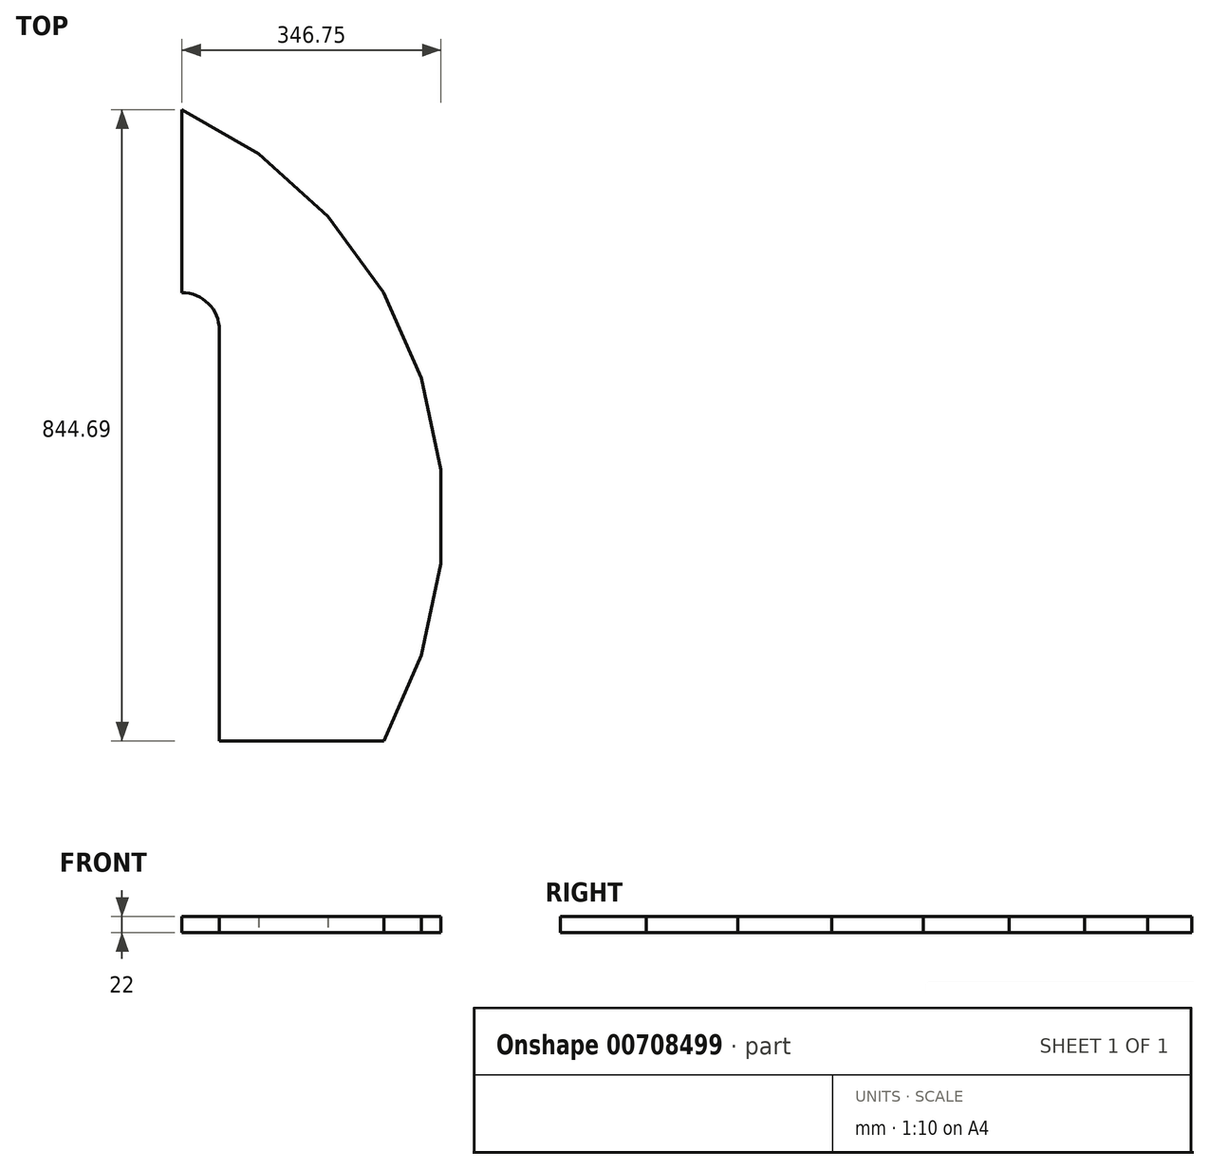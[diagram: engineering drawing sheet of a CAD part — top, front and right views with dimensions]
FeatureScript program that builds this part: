
annotation { "Feature Type Name" : "Feature", "Feature Type Description" : "" }
export const myFeature = defineFeature(function(context is Context, id is Id, definition is map)
    precondition{}
    {
        {
            var Q0;
            Q0=qCreatedBy(makeId("Top.planeOp"),FACE);
            var sketch = newSketch(context, id + "F0", { "sketchPlane" : qUnion([Q0])});
            skLineSegment(sketch, "E0.right", {"start": v(300, -300) * mm, "end": v(300, 250) * mm});
            skPoint(sketch, "E0.middle", {"position": v(0, 0) * mm});
            skPoint(sketch, "E1.end.orphan", {"position": v(-300, -300) * mm});
            skLineSegment(sketch, "E2.22", {"start": v(250, 544.7) * mm, "end": v(352.35, 485.7) * mm});
            skLineSegment(sketch, "E2.23", {"start": v(352.35, 485.7) * mm, "end": v(445.67, 401.78) * mm});
            skLineSegment(sketch, "E2.24", {"start": v(445.67, 401.78) * mm, "end": v(519.49, 300.29) * mm});
            skLineSegment(sketch, "E2.25", {"start": v(519.49, 300.29) * mm, "end": v(570.58, 185.66) * mm});
            skLineSegment(sketch, "E2.26", {"start": v(570.58, 185.66) * mm, "end": v(596.71, 62.9) * mm});
            skLineSegment(sketch, "E2.27", {"start": v(596.71, 62.9) * mm, "end": v(596.75, -62.6) * mm});
            skLineSegment(sketch, "E2.28", {"start": v(596.75, -62.6) * mm, "end": v(570.66, -185.35) * mm});
            skPoint(sketch, "E3.visualSharp", {"position": v(-300, 300) * mm});
            skPoint(sketch, "E4.visualSharp", {"position": v(-300, -52.1) * mm});
            skPoint(sketch, "E5.visualSharp", {"position": v(300, 300) * mm});
            skArc(sketch, "E5.filletArc", {"start": v(300, 250) * mm, "mid": v(285.36, 285.36) * mm, "end": v(250, 300) * mm});
            skLineSegment(sketch, "E6", {"start": v(300, -300) * mm, "end": v(520, -300) * mm});
            skLineSegment(sketch, "E7", {"start": v(570.66, -185.35) * mm, "end": v(520, -300) * mm});
            skLineSegment(sketch, "E8", {"start": v(-300, -2.1) * mm, "end": v(-300, -2.1) * mm});
            skLineSegment(sketch, "E9", {"start": v(250, 300) * mm, "end": v(250, 544.7) * mm});
            skPoint(sketch, "E10.orphan", {"position": v(243.62, 548.37) * mm});
            skSolve(sketch);
        }
        {
            var Q0;
            Q0=qSketchRegion(id+"F0",true);
            extrude(context, id + "F1", {"entities" : qUnion([Q0]), "depth" : 22 * mm, "offsetDistance" : 25 * mm});
        }
    });
